# Revit family: 1METALFIRE_AVENUE_PLUS_MF_GHE_1S
name_source: partatom
category: Mechanical Equipment
revit_build: Autodesk Revit 2017 (Build: 20160225_1515(x64)
units: mm (PartAtom-declared; Revit-internal decimal feet)

## family parameters
Always vertical = Yes
Cut with Voids When Loaded = No
Host = Wall
OmniClass Number = 23.75.00.00
OmniClass Title = Climate Control (HVAC)
Part Type = Normal
Room Calculation Point = Yes
Round Connector Dimension = Use Diameter
Shared = No

## types (2) — shared parameters
BIM BADGE = https://bim.archiproducts.com
Description = The Avenue plus represents the latest generation of closed gas-fired fireplaces. Although the output is lower than the Avenue series, the Avenue plus achieves the highest efficiency in the Metalfire range, 90%.
EFFICIENCY = 90.00%
ENERGY EFFICIENCY CLASS = A (G20) / B (G30)
FINISHING MATERIAL = Black painted vermiculite plates - Metalfire
FRAME MATERIAL = Iron - Metalfire
MATERIAL DESCRIPTION = Iron, galvanized steel and vermiculite plates
Manufacturer = Metalfire
Model = Avenue Plus
OVERALL DEPTH = 444 mm
PRODUCT SHEET = https://www.archiproducts.com
SMOKE EXHAUST = Ø100/150 mm
TECHNICAL SHEET = https://www.metalfire.eu
URL = https://www.metalfire.eu
WEIGHT = 100.00 kg

## per-type parameters (varying)
| type | HEIGHT | OUTPUT | OVERALL HEIGHT | OVERALL WIDTH | PRODUCT CODE | WIDTH |
| 700 x 600 mm | 590 mm | 5.8 kW | 970 mm | 828 mm | MF 700-60 GHE 1S | 700 mm |
| 800 x 400 mm | 390 mm | 5.5 kW | 770 mm | 928 mm | MF 800-40 GHE 1S | 800 mm |

## geometry (parser evidence)
native form markers: Sweep x3
no freeform markers — native parametric forms only
